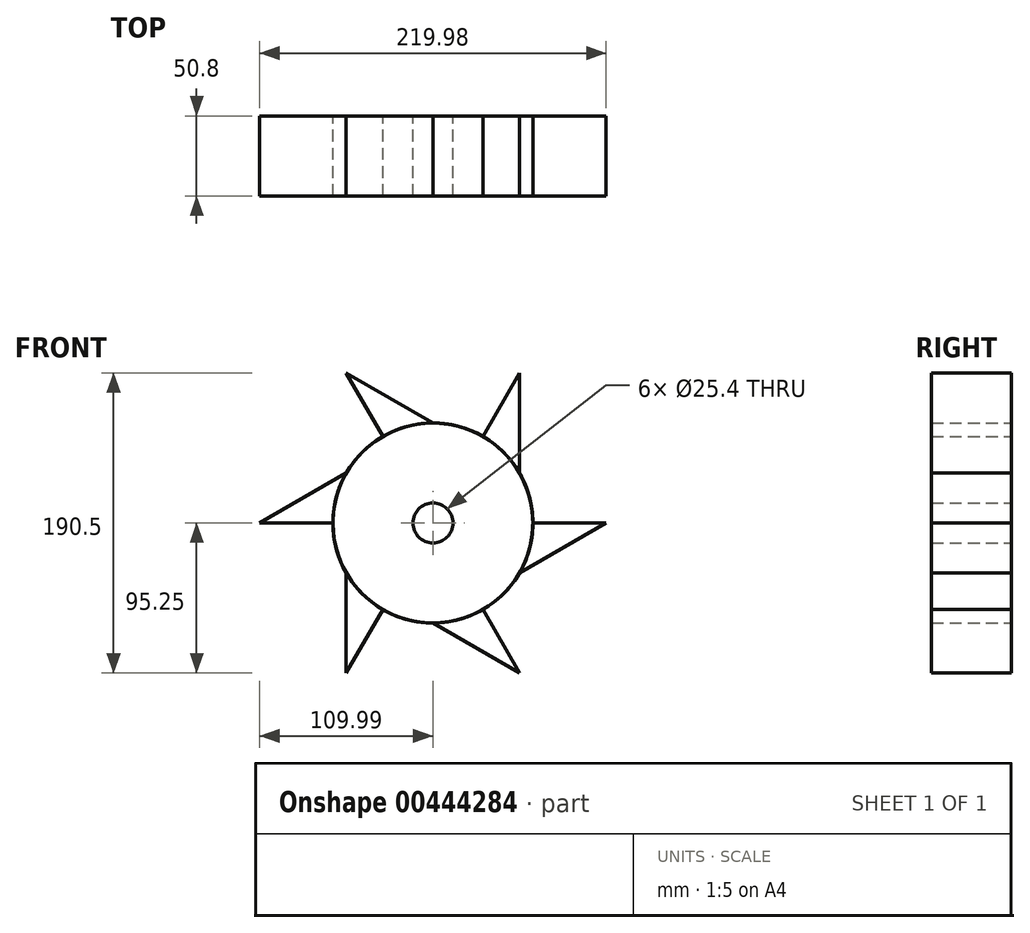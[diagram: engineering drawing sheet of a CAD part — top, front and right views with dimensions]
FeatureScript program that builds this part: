
annotation { "Feature Type Name" : "Feature", "Feature Type Description" : "" }
export const myFeature = defineFeature(function(context is Context, id is Id, definition is map)
    precondition{}
    {
        {
            var Q0;
            Q0=qCreatedBy(makeId("Front.planeOp"),FACE);
            var sketch = newSketch(context, id + "F0", { "sketchPlane" : qUnion([Q0])});
            skCircle(sketch, "E0", {"center": v(0, 0) * mm, "radius": 63.5 * mm});
            skCircle(sketch, "E1", {"center": v(0, 0) * mm, "radius": 12.7 * mm});
            skSolve(sketch);
        }
        {
            var Q0;
            Q0 = qSketchRegion(id + "F0", true);
            extrude(context, id + "F1", {"entities" : qUnion([Q0]), "depth" : 25.4 * mm, "hasSecondDirection" : true, "secondDirectionOppositeDirection" : true, "secondDirectionDepth" : 25.4 * mm});
        }
        {
            var Q0;
            Q0=qCreatedBy(makeId("Front.planeOp"),FACE);
            var sketch = newSketch(context, id + "F2", { "sketchPlane" : qUnion([Q0])});
            skLineSegment(sketch, "E2", {"start": v(63.5, 0) * mm, "end": v(109.99, 0) * mm});
            skLineSegment(sketch, "E3", {"start": v(109.99, 0) * mm, "end": v(55, -31.75) * mm});
            skLineSegment(sketch, "E4", {"start": v(55, -31.75) * mm, "end": v(63.5, 0) * mm});
            skLineSegment(sketch, "E5", {"start": v(0, 0) * mm, "end": v(55, -31.75) * mm});
            skSolve(sketch);
        }
        {
            var Q0;
            Q0=makeQuery(id+"F2.imprint","IMPRINT",FACE,{"disambiguationData":[TD([[makeQuery(id+"F2.imprint","IMPRINT",EDGE,{"derivedFrom":sQuery(id+"F2.wireOp",EDGE,"E2")}),-1.0]])]});
            extrude(context, id + "F3", {"entities" : qUnion([Q0]), "operationType" : NewBodyOperationType.ADD, "depth" : 25.4 * mm, "hasSecondDirection" : true, "secondDirectionOppositeDirection" : true, "secondDirectionDepth" : 25.4 * mm});
        }
        {
            var Q0;
            Q0=makeQuery(id+"F1.opExtrude","SWEPT_BODY",BODY,{"disambiguationData":[OSD([sQuery(id+"F0.wireOp",EDGE,"E0"),sQuery(id+"F0.wireOp",EDGE,"E1")])]});
            var Q1;
            Q1=makeQuery(id+"F1.opExtrude","CAP_EDGE",EDGE,{"disambiguationData":[OSD([sQuery(id+"F0.wireOp",EDGE,"E1")])],"isStart":false});
            circularPattern(context, id + "F4", {"entities" : qUnion([Q0]), "axis" : qUnion([Q1]), "angle" : 360 * degree, "instanceCount" : 6, "equalSpace" : true});
        }
    });
